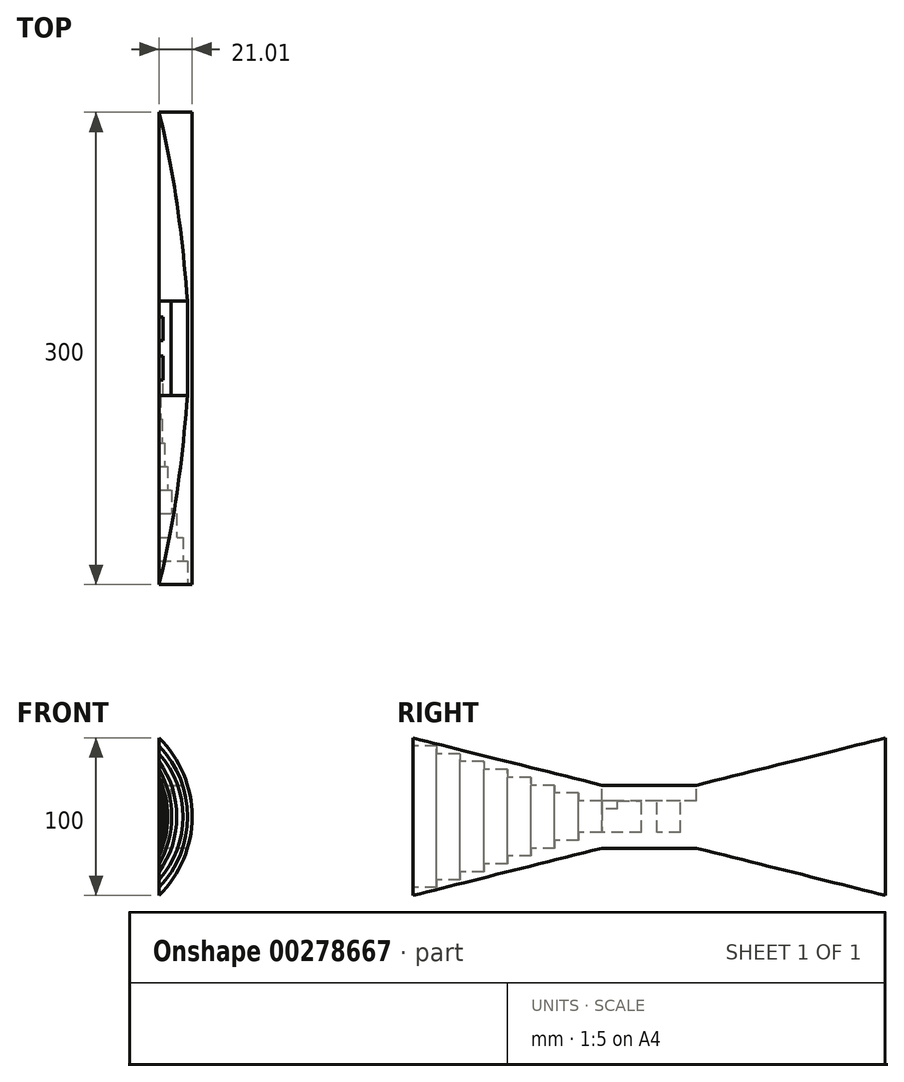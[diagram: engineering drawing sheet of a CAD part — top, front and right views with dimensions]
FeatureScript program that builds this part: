
annotation { "Feature Type Name" : "Feature", "Feature Type Description" : "" }
export const myFeature = defineFeature(function(context is Context, id is Id, definition is map)
    precondition{}
    {
        {
            var Q0;
            Q0=qCreatedBy(makeId("Front.planeOp"),FACE);
            var sketch = newSketch(context, id + "F0", { "sketchPlane" : qUnion([Q0])});
            skLineSegment(sketch, "E0.bottom", {"start": v(-12.5, 50) * mm, "end": v(12.5, 50) * mm});
            skLineSegment(sketch, "E0.top", {"start": v(-12.5, -50) * mm, "end": v(12.5, -50) * mm});
            skLineSegment(sketch, "E0.left", {"start": v(-12.5, 50) * mm, "end": v(-12.5, -50) * mm});
            skLineSegment(sketch, "E0.right", {"start": v(12.5, 50) * mm, "end": v(12.5, -50) * mm});
            skSolve(sketch);
        }
        {
            var Q0;
            Q0 = qSketchRegion(id + "F0", true);
            extrude(context, id + "F1", {"entities" : qUnion([Q0]), "depth" : 300 * mm});
        }
        {
            var Q0;
            Q0=makeQuery(id+"F1.opExtrude","SWEPT_FACE",FACE,{"disambiguationData":[OSD([sQuery(id+"F0.wireOp",EDGE,"E0.right")])]});
            var sketch = newSketch(context, id + "F2", { "sketchPlane" : qUnion([Q0])});
            skLineSegment(sketch, "E1", {"start": v(-120, 20) * mm, "end": v(-180, 20) * mm});
            skLineSegment(sketch, "E2", {"start": v(-180, 20) * mm, "end": v(-300, 50) * mm});
            skLineSegment(sketch, "E3", {"start": v(-300, 50) * mm, "end": v(0, 50) * mm});
            skLineSegment(sketch, "E4", {"start": v(0, 50) * mm, "end": v(-120, 20) * mm});
            skSolve(sketch);
        }
        {
            var Q0;
            Q0 = qSketchRegion(id + "F2", true);
            extrude(context, id + "F3", {"entities" : qUnion([Q0]), "operationType" : NewBodyOperationType.REMOVE, "oppositeDirection" : true, "depth" : 80 * mm});
        }
        {
            var Q0;
            Q0=makeQuery(id+"F1.opExtrude","SWEPT_FACE",FACE,{"disambiguationData":[OSD([sQuery(id+"F0.wireOp",EDGE,"E0.left")])]});
            var sketch = newSketch(context, id + "F4", { "sketchPlane" : qUnion([Q0])});
            skLineSegment(sketch, "E5", {"start": v(120, -20) * mm, "end": v(180, -20) * mm});
            skLineSegment(sketch, "E6", {"start": v(180, -20) * mm, "end": v(300, -50) * mm});
            skLineSegment(sketch, "E7", {"start": v(300, -50) * mm, "end": v(0, -50) * mm});
            skLineSegment(sketch, "E8", {"start": v(0, -50) * mm, "end": v(120, -20) * mm});
            skSolve(sketch);
        }
        {
            var Q0;
            Q0 = qSketchRegion(id + "F4", true);
            extrude(context, id + "F5", {"entities" : qUnion([Q0]), "operationType" : NewBodyOperationType.REMOVE, "oppositeDirection" : true, "depth" : 80 * mm});
        }
        {
            var Q0;
            Q0=makeQuery(id+"F1.opExtrude","CAP_FACE",FACE,{"disambiguationData":[OSD([sQuery(id+"F0.wireOp",EDGE,"E0.bottom"),sQuery(id+"F0.wireOp",EDGE,"E0.top"),sQuery(id+"F0.wireOp",EDGE,"E0.left"),sQuery(id+"F0.wireOp",EDGE,"E0.right")])],"isStart":false});
            var sketch = newSketch(context, id + "F6", { "sketchPlane" : qUnion([Q0])});
            skArc(sketch, "E9", {"start": v(-12.5, -45) * mm, "mid": v(5.6, 0) * mm, "end": v(-12.5, 45) * mm});
            skLineSegment(sketch, "E10", {"start": v(-12.5, 45) * mm, "end": v(-12.5, -45) * mm});
            skSolve(sketch);
        }
        {
            var Q0;
            Q0 = qSketchRegion(id + "F6", true);
            extrude(context, id + "F7", {"entities" : qUnion([Q0]), "operationType" : NewBodyOperationType.REMOVE, "oppositeDirection" : true, "depth" : 15 * mm});
        }
        {
            var Q0;
            Q0=makeQuery(id+"F7.boolean.opBoolean","COPY",FACE,{"derivedFrom":makeQuery(id+"F7.opExtrude","CAP_FACE",FACE,{"disambiguationData":[OSD([sQuery(id+"F6.wireOp",EDGE,"E9"),sQuery(id+"F6.wireOp",EDGE,"E10")])],"isStart":false})});
            var sketch = newSketch(context, id + "F8", { "sketchPlane" : qUnion([Q0])});
            skArc(sketch, "E11", {"start": v(-12.5, -40) * mm, "mid": v(2.78, 0) * mm, "end": v(-12.5, 40) * mm});
            skLineSegment(sketch, "E12", {"start": v(-12.5, 40) * mm, "end": v(-12.5, -40) * mm});
            skSolve(sketch);
        }
        {
            var Q0;
            Q0 = qSketchRegion(id + "F8", true);
            extrude(context, id + "F9", {"entities" : qUnion([Q0]), "operationType" : NewBodyOperationType.REMOVE, "oppositeDirection" : true, "depth" : 15 * mm});
        }
        {
            var Q0;
            Q0=makeQuery(id+"F9.boolean.opBoolean","COPY",FACE,{"derivedFrom":makeQuery(id+"F9.opExtrude","CAP_FACE",FACE,{"disambiguationData":[OSD([sQuery(id+"F8.wireOp",EDGE,"E11"),sQuery(id+"F8.wireOp",EDGE,"E12")])],"isStart":false})});
            var sketch = newSketch(context, id + "F10", { "sketchPlane" : qUnion([Q0])});
            skArc(sketch, "E13", {"start": v(-12.5, -35) * mm, "mid": v(-1.23, 0) * mm, "end": v(-12.5, 35) * mm});
            skLineSegment(sketch, "E14", {"start": v(-12.5, 35) * mm, "end": v(-12.5, -35) * mm});
            skSolve(sketch);
        }
        {
            var Q0;
            Q0 = qSketchRegion(id + "F10", true);
            extrude(context, id + "F11", {"entities" : qUnion([Q0]), "operationType" : NewBodyOperationType.REMOVE, "oppositeDirection" : true, "depth" : 15 * mm});
        }
        {
            var Q0;
            Q0=makeQuery(id+"F11.boolean.opBoolean","COPY",FACE,{"derivedFrom":makeQuery(id+"F11.opExtrude","CAP_FACE",FACE,{"disambiguationData":[OSD([sQuery(id+"F10.wireOp",EDGE,"E13"),sQuery(id+"F10.wireOp",EDGE,"E14")])],"isStart":false})});
            var sketch = newSketch(context, id + "F12", { "sketchPlane" : qUnion([Q0])});
            skArc(sketch, "E15", {"start": v(-12.5, -30) * mm, "mid": v(-4.46, 0) * mm, "end": v(-12.5, 30) * mm});
            skLineSegment(sketch, "E16", {"start": v(-12.5, 30) * mm, "end": v(-12.5, -30) * mm});
            skSolve(sketch);
        }
        {
            var Q0;
            Q0 = qSketchRegion(id + "F12", true);
            extrude(context, id + "F13", {"entities" : qUnion([Q0]), "operationType" : NewBodyOperationType.REMOVE, "oppositeDirection" : true, "depth" : 15 * mm});
        }
        {
            var Q0;
            Q0=makeQuery(id+"F13.boolean.opBoolean","COPY",FACE,{"derivedFrom":makeQuery(id+"F13.opExtrude","CAP_FACE",FACE,{"disambiguationData":[OSD([sQuery(id+"F12.wireOp",EDGE,"E15"),sQuery(id+"F12.wireOp",EDGE,"E16")])],"isStart":false})});
            var sketch = newSketch(context, id + "F14", { "sketchPlane" : qUnion([Q0])});
            skArc(sketch, "E17", {"start": v(-12.5, -25) * mm, "mid": v(-7.04, 0) * mm, "end": v(-12.5, 25) * mm});
            skLineSegment(sketch, "E18", {"start": v(-12.5, 25) * mm, "end": v(-12.5, -25) * mm});
            skSolve(sketch);
        }
        {
            var Q0;
            Q0 = qSketchRegion(id + "F14", true);
            extrude(context, id + "F15", {"entities" : qUnion([Q0]), "operationType" : NewBodyOperationType.REMOVE, "oppositeDirection" : true, "depth" : 15 * mm});
        }
        {
            var Q0;
            Q0=makeQuery(id+"F15.boolean.opBoolean","COPY",FACE,{"derivedFrom":makeQuery(id+"F15.opExtrude","CAP_FACE",FACE,{"disambiguationData":[OSD([sQuery(id+"F14.wireOp",EDGE,"E17"),sQuery(id+"F14.wireOp",EDGE,"E18")])],"isStart":false})});
            var sketch = newSketch(context, id + "F16", { "sketchPlane" : qUnion([Q0])});
            skPoint(sketch, "E19.end.orphan", {"position": v(-12.5, 20) * mm});
            skPoint(sketch, "E19.start.orphan", {"position": v(-12.5, -20) * mm});
            skArc(sketch, "E20", {"start": v(-12.5, -20) * mm, "mid": v(-9.07, 0) * mm, "end": v(-12.5, 20) * mm});
            skLineSegment(sketch, "E21", {"start": v(-12.5, 20) * mm, "end": v(-12.5, -20) * mm});
            skSolve(sketch);
        }
        {
            var Q0;
            Q0 = qSketchRegion(id + "F16", true);
            extrude(context, id + "F17", {"entities" : qUnion([Q0]), "operationType" : NewBodyOperationType.REMOVE, "oppositeDirection" : true, "depth" : 15 * mm});
        }
        {
            var Q0;
            Q0=makeQuery(id+"F17.boolean.opBoolean","COPY",FACE,{"derivedFrom":makeQuery(id+"F17.opExtrude","CAP_FACE",FACE,{"disambiguationData":[OSD([sQuery(id+"F16.wireOp",EDGE,"E20"),sQuery(id+"F16.wireOp",EDGE,"E21")])],"isStart":false})});
            var sketch = newSketch(context, id + "F18", { "sketchPlane" : qUnion([Q0])});
            skArc(sketch, "E22", {"start": v(-12.5, -15) * mm, "mid": v(-10.6, 0) * mm, "end": v(-12.5, 15) * mm});
            skLineSegment(sketch, "E23", {"start": v(-12.5, 15) * mm, "end": v(-12.5, -15) * mm});
            skSolve(sketch);
        }
        {
            var Q0;
            Q0 = qSketchRegion(id + "F18", true);
            extrude(context, id + "F19", {"entities" : qUnion([Q0]), "operationType" : NewBodyOperationType.REMOVE, "oppositeDirection" : true, "depth" : 15 * mm});
        }
        {
            var Q0;
            Q0=makeQuery(id+"F19.boolean.opBoolean","COPY",FACE,{"derivedFrom":makeQuery(id+"F19.opExtrude","CAP_FACE",FACE,{"disambiguationData":[OSD([sQuery(id+"F18.wireOp",EDGE,"E22"),sQuery(id+"F18.wireOp",EDGE,"E23")])],"isStart":false})});
            var sketch = newSketch(context, id + "F20", { "sketchPlane" : qUnion([Q0])});
            skArc(sketch, "E24", {"start": v(-12.5, -10) * mm, "mid": v(-11.66, 0) * mm, "end": v(-12.5, 10) * mm});
            skLineSegment(sketch, "E25", {"start": v(-12.5, 10) * mm, "end": v(-12.5, -10) * mm});
            skSolve(sketch);
        }
        {
            var Q0;
            Q0 = qSketchRegion(id + "F20", true);
            extrude(context, id + "F21", {"entities" : qUnion([Q0]), "operationType" : NewBodyOperationType.REMOVE, "oppositeDirection" : true, "depth" : 15 * mm});
        }
        {
            var Q0;
            Q0=makeQuery(id+"F1.opExtrude","CAP_FACE",FACE,{"disambiguationData":[OSD([sQuery(id+"F0.wireOp",EDGE,"E0.bottom"),sQuery(id+"F0.wireOp",EDGE,"E0.top"),sQuery(id+"F0.wireOp",EDGE,"E0.left"),sQuery(id+"F0.wireOp",EDGE,"E0.right")])],"isStart":false});
            var sketch = newSketch(context, id + "F22", { "sketchPlane" : qUnion([Q0])});
            skLineSegment(sketch, "E26", {"start": v(-12.5, 50) * mm, "end": v(12.5, 50) * mm});
            skLineSegment(sketch, "E27", {"start": v(12.5, 50) * mm, "end": v(12.5, -50) * mm});
            skPoint(sketch, "E28.end.orphan", {"position": v(0, -50) * mm});
            skLineSegment(sketch, "E29", {"start": v(12.5, -50) * mm, "end": v(-12.5, -50) * mm});
            skArc(sketch, "E30", {"start": v(-12.5, -50) * mm, "mid": v(8.51, 0) * mm, "end": v(-12.5, 50) * mm});
            skSolve(sketch);
        }
        {
            var Q0;
            Q0 = qSketchRegion(id + "F22", true);
            extrude(context, id + "F23", {"entities" : qUnion([Q0]), "operationType" : NewBodyOperationType.REMOVE, "oppositeDirection" : true, "depth" : 300 * mm});
        }
        {
            var Q0;
            Q0=makeQuery(id+"F3.boolean.opBoolean","COPY",FACE,{"derivedFrom":makeQuery(id+"F3.opExtrude","SWEPT_FACE",FACE,{"disambiguationData":[OSD([sQuery(id+"F2.wireOp",EDGE,"E1")])]})});
            var sketch = newSketch(context, id + "F24", { "sketchPlane" : qUnion([Q0])});
            skLineSegment(sketch, "E31.bottom", {"start": v(-12.5, -120) * mm, "end": v(-5, -120) * mm});
            skLineSegment(sketch, "E31.top", {"start": v(-12.5, -180) * mm, "end": v(-5, -180) * mm});
            skLineSegment(sketch, "E31.left", {"start": v(-12.5, -120) * mm, "end": v(-12.5, -180) * mm});
            skLineSegment(sketch, "E31.right", {"start": v(-5, -120) * mm, "end": v(-5, -180) * mm});
            skSolve(sketch);
        }
        {
            var Q0;
            Q0 = qSketchRegion(id + "F24", true);
            extrude(context, id + "F25", {"entities" : qUnion([Q0]), "operationType" : NewBodyOperationType.REMOVE, "oppositeDirection" : true, "depth" : 10 * mm});
        }
        {
            var Q0;
            Q0=makeQuery(id+"F25.boolean.opBoolean","COPY",FACE,{"derivedFrom":makeQuery(id+"F25.opExtrude","CAP_FACE",FACE,{"disambiguationData":[OSD([sQuery(id+"F24.wireOp",EDGE,"E31.bottom"),sQuery(id+"F24.wireOp",EDGE,"E31.top"),sQuery(id+"F24.wireOp",EDGE,"E31.left"),sQuery(id+"F24.wireOp",EDGE,"E31.right")])],"isStart":false})});
            var sketch = newSketch(context, id + "F26", { "sketchPlane" : qUnion([Q0])});
            skLineSegment(sketch, "E32.bottom", {"start": v(-12.5, -170) * mm, "end": v(-10, -170) * mm});
            skLineSegment(sketch, "E32.top", {"start": v(-12.5, -155) * mm, "end": v(-10, -155) * mm});
            skLineSegment(sketch, "E32.left", {"start": v(-12.5, -170) * mm, "end": v(-12.5, -155) * mm});
            skLineSegment(sketch, "E32.right", {"start": v(-10, -170) * mm, "end": v(-10, -155) * mm});
            skLineSegment(sketch, "E33.bottom", {"start": v(-12.5, -130) * mm, "end": v(-10, -130) * mm});
            skLineSegment(sketch, "E33.top", {"start": v(-12.5, -145) * mm, "end": v(-10, -145) * mm});
            skLineSegment(sketch, "E33.left", {"start": v(-12.5, -130) * mm, "end": v(-12.5, -145) * mm});
            skLineSegment(sketch, "E33.right", {"start": v(-10, -130) * mm, "end": v(-10, -145) * mm});
            skSolve(sketch);
        }
        {
            var Q0;
            Q0 = qSketchRegion(id + "F26", true);
            extrude(context, id + "F27", {"entities" : qUnion([Q0]), "operationType" : NewBodyOperationType.REMOVE, "oppositeDirection" : true, "depth" : 20 * mm});
        }
        {
            var Q0;
            {var subQ2=sQuery(id+"F0.wireOp",EDGE,"E0.left");var subQ14=makeQuery(id+"F1.opExtrude","SWEPT_FACE",FACE,{"disambiguationData":[OSD([subQ2])]});Q0=makeQuery(id+"F25.boolean.opBoolean","SPLIT",FACE,{"disambiguationData":[TD([makeQuery(id+"F3.boolean.opBoolean","COPY",FACE,{"derivedFrom":makeQuery(id+"F3.opExtrude","SWEPT_FACE",FACE,{"disambiguationData":[OSD([sQuery(id+"F2.wireOp",EDGE,"E4")])]})})])],"derivedFrom":subQ14});}
            var sketch = newSketch(context, id + "F28", { "sketchPlane" : qUnion([Q0])});
            skLineSegment(sketch, "E34.bottom", {"start": v(170, -10) * mm, "end": v(180, -10) * mm});
            skLineSegment(sketch, "E34.top", {"start": v(170, 5) * mm, "end": v(180, 5) * mm});
            skLineSegment(sketch, "E34.left", {"start": v(170, -10) * mm, "end": v(170, 5) * mm});
            skLineSegment(sketch, "E34.right", {"start": v(180, -10) * mm, "end": v(180, 5) * mm});
            skSolve(sketch);
        }
        {
            var Q0;
            Q0 = qSketchRegion(id + "F28", true);
            extrude(context, id + "F29", {"entities" : qUnion([Q0]), "operationType" : NewBodyOperationType.REMOVE, "oppositeDirection" : true, "depth" : 2.5 * mm});
        }
        {
            var Q0;
            Q0=qCreatedBy(makeId("Front.planeOp"),FACE);
            cPlane(context, id + "F30", {"entities" : qUnion([Q0]), "cplaneType" : CPlaneType.OFFSET, "offset" : 150 * mm, "width" : 150 * mm, "height" : 150 * mm});
        }
    });
